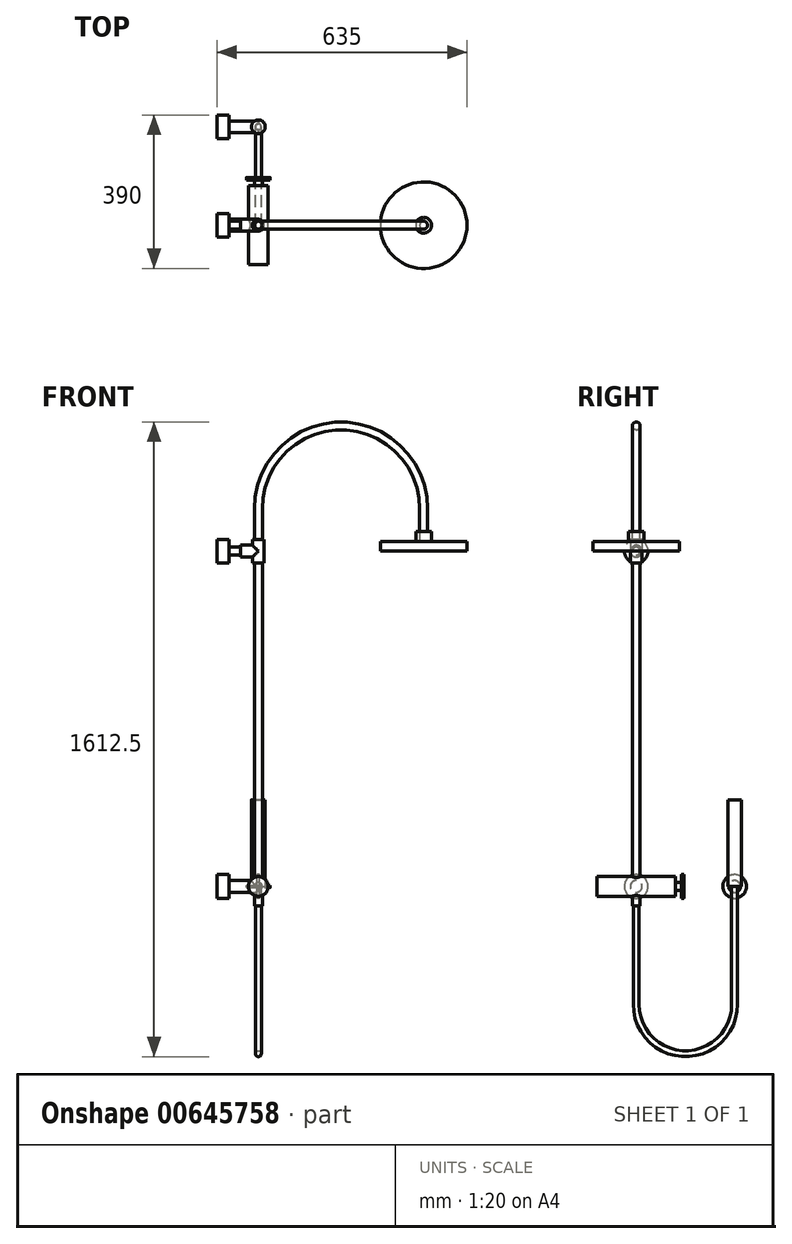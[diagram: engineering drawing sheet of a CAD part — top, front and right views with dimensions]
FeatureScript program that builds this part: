
annotation { "Feature Type Name" : "Feature", "Feature Type Description" : "" }
export const myFeature = defineFeature(function(context is Context, id is Id, definition is map)
    precondition{}
    {
        {
            var Q0;
            Q0=qCreatedBy(makeId("Front.planeOp"),FACE);
            var sketch = newSketch(context, id + "F0", { "sketchPlane" : qUnion([Q0])});
            skLineSegment(sketch, "E0", {"start": v(0, 0) * mm, "end": v(0, 960) * mm});
            skArc(sketch, "E1", {"start": v(420, 960) * mm, "mid": v(210, 1170) * mm, "end": v(0, 960) * mm});
            skLineSegment(sketch, "E2", {"start": v(210, 1170) * mm, "end": v(-729.28, 1170) * mm, "construction": true});
            skLineSegment(sketch, "E3", {"start": v(420, 960) * mm, "end": v(420, 852) * mm});
            skSolve(sketch);
        }
        {
            var Q0;
            Q0=qCreatedBy(makeId("Top.planeOp"),FACE);
            var sketch = newSketch(context, id + "F1", { "sketchPlane" : qUnion([Q0])});
            skCircle(sketch, "E4", {"center": v(0, 0) * mm, "radius": 10 * mm});
            skSolve(sketch);
        }
        {
            var Q0;
            Q0=qSketchRegion(id+"F1",true);
            var Q1;
            Q1=qConstructionFilter(qBodyType(qCreatedBy(id+"F0",EDGE),BodyType.WIRE),ConstructionObject.NO);
            sweep(context, id + "F2", {"profiles" : qUnion([Q0]), "path" : qUnion([Q1])});
        }
        {
            var Q0;
            Q0=qCreatedBy(makeId("Top.planeOp"),FACE);
            cPlane(context, id + "F3", {"entities" : qUnion([Q0]), "cplaneType" : CPlaneType.OFFSET, "offset" : 852 * mm, "width" : 150 * mm, "height" : 150 * mm});
        }
        {
            var Q0;
            Q0=qCreatedBy(id+"F3.planeOp",FACE);
            var sketch = newSketch(context, id + "F4", { "sketchPlane" : qUnion([Q0])});
            skCircle(sketch, "E5", {"center": v(420, 0) * mm, "radius": 110 * mm});
            skCircle(sketch, "E6.0", {"center": v(420, 0) * mm, "radius": 10 * mm, "construction": true});
            skSolve(sketch);
        }
        {
            var Q0;
            Q0=qSketchRegion(id+"F4",true);
            extrude(context, id + "F5", {"entities" : qUnion([Q0]), "depth" : 25 * mm});
        }
        {
            var Q0;
            Q0=makeQuery(id+"F5.opExtrude","CAP_FACE",FACE,{"disambiguationData":[OSD([sQuery(id+"F4.wireOp",EDGE,"E5")])],"isStart":false});
            var sketch = newSketch(context, id + "F6", { "sketchPlane" : qUnion([Q0])});
            skCircle(sketch, "E7", {"center": v(420, 0) * mm, "radius": 20 * mm});
            skSolve(sketch);
        }
        {
            var Q0;
            Q0=qSketchRegion(id+"F6",true);
            extrude(context, id + "F7", {"entities" : qUnion([Q0]), "depth" : 25 * mm});
        }
        {
            var Q0;
            Q0=qCreatedBy(makeId("Front.planeOp"),FACE);
            var sketch = newSketch(context, id + "F8", { "sketchPlane" : qUnion([Q0])});
            skCircle(sketch, "E8", {"center": v(0, 0) * mm, "radius": 25 * mm});
            skSolve(sketch);
        }
        {
            var Q0;
            Q0=qSketchRegion(id+"F8",true);
            extrude(context, id + "F9", {"entities" : qUnion([Q0]), "operationType" : NewBodyOperationType.ADD, "depth" : 100 * mm});
        }
        {
            var Q0;
            Q0=qSketchRegion(id+"F8",true);
            extrude(context, id + "F10", {"entities" : qUnion([Q0]), "operationType" : NewBodyOperationType.ADD, "oppositeDirection" : true, "depth" : 100 * mm});
        }
        {
            var Q0;
            Q0=makeQuery(id+"F10.opExtrude","CAP_FACE",FACE,{"disambiguationData":[OSD([sQuery(id+"F8.wireOp",EDGE,"E8")])],"isStart":false});
            var sketch = newSketch(context, id + "F11", { "sketchPlane" : qUnion([Q0])});
            skCircle(sketch, "E9", {"center": v(0, 0) * mm, "radius": 10 * mm});
            skSolve(sketch);
        }
        {
            var Q0;
            Q0=qSketchRegion(id+"F11",true);
            extrude(context, id + "F12", {"entities" : qUnion([Q0]), "operationType" : NewBodyOperationType.ADD, "depth" : 15 * mm});
        }
        {
            var Q0;
            Q0=qCreatedBy(makeId("Front.planeOp"),FACE);
            cPlane(context, id + "F13", {"entities" : qUnion([Q0]), "cplaneType" : CPlaneType.OFFSET, "offset" : 118 * mm, "oppositeDirection" : true, "width" : 150 * mm, "height" : 150 * mm});
        }
        {
            var Q0;
            Q0=qCreatedBy(id+"F13.planeOp",FACE);
            var sketch = newSketch(context, id + "F14", { "sketchPlane" : qUnion([Q0])});
            skLineSegment(sketch, "E10", {"start": v(0, 39.33) * mm, "end": v(0, -42.36) * mm, "construction": true});
            skLineSegment(sketch, "E11", {"start": v(-45.91, 0) * mm, "end": v(51.91, 0) * mm, "construction": true});
            skLineSegment(sketch, "E12.bottom", {"start": v(0, 30) * mm, "end": v(3, 30) * mm});
            skLineSegment(sketch, "E12.top", {"start": v(0, 0) * mm, "end": v(3, 0) * mm});
            skLineSegment(sketch, "E12.left", {"start": v(0, 30) * mm, "end": v(0, 0) * mm});
            skLineSegment(sketch, "E12.right", {"start": v(3, 30) * mm, "end": v(3, 0) * mm});
            skSolve(sketch);
        }
        {
            var Q0;
            Q0=qCreatedBy(id+"F13.planeOp",FACE);
            var sketch = newSketch(context, id + "F15", { "sketchPlane" : qUnion([Q0])});
            skLineSegment(sketch, "E13", {"start": v(0, 62.31) * mm, "end": v(0, -98.22) * mm});
            skSolve(sketch);
        }
        {
            var Q0;
            Q0=qSketchRegion(id+"F14",true);
            var Q1;
            Q1=sQuery(id+"F15.wireOp",EDGE,"E13");
            revolve(context, id + "F16", {"operationType" : NewBodyOperationType.ADD, "entities" : qUnion([Q0]), "axis" : qUnion([Q1]), "revolveType" : RevolveType.FULL});
        }
        {
            var Q0;
            Q0=qCreatedBy(id+"F13.planeOp",FACE);
            var sketch = newSketch(context, id + "F17", { "sketchPlane" : qUnion([Q0])});
            skLineSegment(sketch, "E14", {"start": v(0, -8.14) * mm, "end": v(0, 4.33) * mm, "construction": true});
            skLineSegment(sketch, "E15.bottom", {"start": v(0, 0) * mm, "end": v(-3, 0) * mm});
            skLineSegment(sketch, "E15.top", {"start": v(0, -30) * mm, "end": v(-3, -30) * mm});
            skLineSegment(sketch, "E15.left", {"start": v(0, 0) * mm, "end": v(0, -30) * mm});
            skLineSegment(sketch, "E15.right", {"start": v(-3, 0) * mm, "end": v(-3, -30) * mm});
            skSolve(sketch);
        }
        {
            var Q0;
            Q0=qSketchRegion(id+"F17",true);
            var Q1;
            Q1=sQuery(id+"F17.wireOp",EDGE,"E15.left");
            revolve(context, id + "F18", {"entities" : qUnion([Q0]), "axis" : qUnion([Q1]), "revolveType" : RevolveType.FULL});
        }
        {
            var Q0;
            Q0=qCreatedBy(id+"F13.planeOp",FACE);
            var sketch = newSketch(context, id + "F19", { "sketchPlane" : qUnion([Q0])});
            skLineSegment(sketch, "E16", {"start": v(19.86, 0) * mm, "end": v(-126.73, 0) * mm, "construction": true});
            skLineSegment(sketch, "E17.bottom", {"start": v(30, 3) * mm, "end": v(-30, 3) * mm});
            skLineSegment(sketch, "E17.top", {"start": v(30, 0) * mm, "end": v(-30, 0) * mm});
            skLineSegment(sketch, "E17.left", {"start": v(30, 3) * mm, "end": v(30, 0) * mm});
            skLineSegment(sketch, "E17.right", {"start": v(-30, 3) * mm, "end": v(-30, 0) * mm});
            skLineSegment(sketch, "E18", {"start": v(0, 0) * mm, "end": v(0, 54.1) * mm, "construction": true});
            skSolve(sketch);
        }
        {
            var Q0;
            Q0=qSketchRegion(id+"F19",true);
            var Q1;
            Q1=sQuery(id+"F19.wireOp",EDGE,"E16");
            revolve(context, id + "F20", {"entities" : qUnion([Q0]), "axis" : qUnion([Q1]), "revolveType" : RevolveType.FULL});
        }
        {
            var Q0;
            Q0=qCreatedBy(makeId("Top.planeOp"),FACE);
            var sketch = newSketch(context, id + "F21", { "sketchPlane" : qUnion([Q0])});
            skCircle(sketch, "E19", {"center": v(0, 0) * mm, "radius": 10 * mm});
            skSolve(sketch);
        }
        {
            var Q0;
            Q0=qSketchRegion(id+"F21",true);
            extrude(context, id + "F22", {"entities" : qUnion([Q0]), "operationType" : NewBodyOperationType.ADD, "oppositeDirection" : true, "depth" : 50 * mm});
        }
        {
            var Q0;
            Q0=makeQuery(id+"F22.opExtrude","CAP_FACE",FACE,{"disambiguationData":[OSD([sQuery(id+"F21.wireOp",EDGE,"E19")])],"isStart":false});
            var sketch = newSketch(context, id + "F23", { "sketchPlane" : qUnion([Q0])});
            skCircle(sketch, "E20", {"center": v(0, 0) * mm, "radius": 7.5 * mm});
            skSolve(sketch);
        }
        {
            var Q0;
            Q0=qCreatedBy(makeId("Right.planeOp"),FACE);
            var sketch = newSketch(context, id + "F24", { "sketchPlane" : qUnion([Q0])});
            skLineSegment(sketch, "E21", {"start": v(0, 0) * mm, "end": v(0, -300) * mm});
            skArc(sketch, "E22", {"start": v(0, -300) * mm, "mid": v(125, -425) * mm, "end": v(250, -300) * mm});
            skLineSegment(sketch, "E23", {"start": v(250, 0) * mm, "end": v(250, -300) * mm});
            skSolve(sketch);
        }
        {
            var Q0;
            Q0=qSketchRegion(id+"F23",true);
            var Q1;
            Q1=qConstructionFilter(qBodyType(qCreatedBy(id+"F24",EDGE),BodyType.WIRE),ConstructionObject.NO);
            sweep(context, id + "F25", {"operationType" : NewBodyOperationType.ADD, "profiles" : qUnion([Q0]), "path" : qUnion([Q1])});
        }
        {
            var Q0;
            Q0=qCreatedBy(makeId("Right.planeOp"),FACE);
            var sketch = newSketch(context, id + "F26", { "sketchPlane" : qUnion([Q0])});
            skCircle(sketch, "E24", {"center": v(0, 0) * mm, "radius": 15 * mm});
            skSolve(sketch);
        }
        {
            var Q0;
            Q0=qSketchRegion(id+"F26",true);
            extrude(context, id + "F27", {"entities" : qUnion([Q0]), "operationType" : NewBodyOperationType.ADD, "oppositeDirection" : true, "depth" : 105 * mm});
        }
        {
            var Q0;
            Q0=makeQuery(id+"F27.opExtrude","CAP_FACE",FACE,{"disambiguationData":[OSD([sQuery(id+"F26.wireOp",EDGE,"E24")])],"isStart":false});
            var sketch = newSketch(context, id + "F28", { "sketchPlane" : qUnion([Q0])});
            skCircle(sketch, "E25", {"center": v(0, 0) * mm, "radius": 30 * mm});
            skSolve(sketch);
        }
        {
            var Q0;
            Q0=qSketchRegion(id+"F28",true);
            extrude(context, id + "F29", {"entities" : qUnion([Q0]), "operationType" : NewBodyOperationType.ADD, "oppositeDirection" : true, "depth" : 30 * mm});
        }
        {
            var Q0;
            Q0=qCreatedBy(id+"F3.planeOp",FACE);
            var sketch = newSketch(context, id + "F30", { "sketchPlane" : qUnion([Q0])});
            skCircle(sketch, "E26", {"center": v(0, 0) * mm, "radius": 15 * mm});
            skSolve(sketch);
        }
        {
            var Q0;
            Q0=qSketchRegion(id+"F30",true);
            extrude(context, id + "F31", {"entities" : qUnion([Q0]), "operationType" : NewBodyOperationType.ADD, "depth" : 30 * mm});
        }
        {
            var Q0;
            Q0=qSketchRegion(id+"F30",true);
            extrude(context, id + "F32", {"entities" : qUnion([Q0]), "operationType" : NewBodyOperationType.ADD, "oppositeDirection" : true, "depth" : 30 * mm});
        }
        {
            var Q0;
            Q0=qCreatedBy(makeId("Right.planeOp"),FACE);
            var sketch = newSketch(context, id + "F33", { "sketchPlane" : qUnion([Q0])});
            skLineSegment(sketch, "E27.0", {"start": v(-110, 852) * mm, "end": v(110, 852) * mm, "construction": true});
            skLineSegment(sketch, "E28.0", {"start": v(-15, 822) * mm, "end": v(15, 822) * mm, "construction": true});
            skLineSegment(sketch, "E29", {"start": v(0, 822) * mm, "end": v(0, 905.09) * mm, "construction": true});
            skCircle(sketch, "E30", {"center": v(0, 852) * mm, "radius": 15 * mm});
            skSolve(sketch);
        }
        {
            var Q0;
            Q0=qSketchRegion(id+"F33",true);
            extrude(context, id + "F34", {"entities" : qUnion([Q0]), "operationType" : NewBodyOperationType.ADD, "oppositeDirection" : true, "depth" : 45 * mm});
        }
        {
            var Q0;
            Q0=makeQuery(id+"F34.opExtrude","CAP_FACE",FACE,{"disambiguationData":[OSD([sQuery(id+"F33.wireOp",EDGE,"E30")])],"isStart":false});
            var sketch = newSketch(context, id + "F35", { "sketchPlane" : qUnion([Q0])});
            skCircle(sketch, "E31", {"center": v(0, 852) * mm, "radius": 10 * mm});
            skSolve(sketch);
        }
        {
            var Q0;
            Q0=qSketchRegion(id+"F35",true);
            extrude(context, id + "F36", {"entities" : qUnion([Q0]), "operationType" : NewBodyOperationType.ADD, "depth" : 30 * mm});
        }
        {
            var Q0;
            Q0=makeQuery(id+"F36.opExtrude","CAP_FACE",FACE,{"disambiguationData":[OSD([sQuery(id+"F35.wireOp",EDGE,"E31")])],"isStart":false});
            var sketch = newSketch(context, id + "F37", { "sketchPlane" : qUnion([Q0])});
            skCircle(sketch, "E32", {"center": v(0, 852) * mm, "radius": 30 * mm});
            skSolve(sketch);
        }
        {
            var Q0;
            Q0=qSketchRegion(id+"F37",true);
            extrude(context, id + "F38", {"entities" : qUnion([Q0]), "operationType" : NewBodyOperationType.ADD, "depth" : 30 * mm});
        }
        {
            var Q0;
            Q0=qCreatedBy(makeId("Front.planeOp"),FACE);
            cPlane(context, id + "F39", {"entities" : qUnion([Q0]), "cplaneType" : CPlaneType.OFFSET, "offset" : 250 * mm, "oppositeDirection" : true, "width" : 150 * mm, "height" : 150 * mm});
        }
        {
            var Q0;
            Q0=qCreatedBy(id+"F39.planeOp",FACE);
            var sketch = newSketch(context, id + "F40", { "sketchPlane" : qUnion([Q0])});
            skLineSegment(sketch, "E33", {"start": v(0, 0) * mm, "end": v(-200, 0) * mm, "construction": true});
            skLineSegment(sketch, "E34", {"start": v(-105, 30) * mm, "end": v(-75, 30) * mm});
            skLineSegment(sketch, "E35", {"start": v(-75, 15) * mm, "end": v(0, 15) * mm});
            skLineSegment(sketch, "E36", {"start": v(-75, 15) * mm, "end": v(-75, 30) * mm});
            skLineSegment(sketch, "E37", {"start": v(-105, 30) * mm, "end": v(-105, 0) * mm});
            skLineSegment(sketch, "E38", {"start": v(-105, 0) * mm, "end": v(0, 0) * mm});
            skLineSegment(sketch, "E39", {"start": v(0, 0) * mm, "end": v(0, 15) * mm});
            skSolve(sketch);
        }
        {
            var Q0;
            Q0=qSketchRegion(id+"F40",true);
            var Q1;
            Q1=sQuery(id+"F40.wireOp",EDGE,"E33");
            revolve(context, id + "F41", {"operationType" : NewBodyOperationType.ADD, "entities" : qUnion([Q0]), "axis" : qUnion([Q1]), "revolveType" : RevolveType.FULL});
        }
        {
            var Q0;
            Q0=makeQuery(id+"F25.opSweep","CAP_FACE",FACE,{"disambiguationData":[OSD([sQuery(id+"F23.wireOp",EDGE,"E20"),sQuery(id+"F24.wireOp",VERTEX,"E23.start")])],"isStart":false});
            var sketch = newSketch(context, id + "F42", { "sketchPlane" : qUnion([Q0])});
            skCircle(sketch, "E40", {"center": v(0, 250) * mm, "radius": 17.5 * mm});
            skSolve(sketch);
        }
        {
            var Q0;
            Q0=qSketchRegion(id+"F42",true);
            extrude(context, id + "F43", {"entities" : qUnion([Q0]), "operationType" : NewBodyOperationType.ADD, "depth" : 220 * mm});
        }
    });
